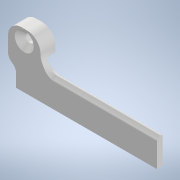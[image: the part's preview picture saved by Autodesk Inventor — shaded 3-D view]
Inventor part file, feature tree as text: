
AUTODESK INVENTOR PART (.ipt)
format: ipt  version: 2022 (Build 260153000, 153)  size: 229,888 bytes
history: native  units: mm
features: reference x7, other x6, fillet x5, extrude x3, sketch x3, chamfer x1, projected_geometry x1
ambient origin geometry x8: Origin, YZ Plane, XZ Plane, XY Plane, X Axis, Y Axis, Z Axis, Center Point
bodies: Body1 (feature_tree)
feature tree (26):
  other  "Твердое тело1"
  extrude  "Выдавливание1"  Depth=1.0mm
  extrude  "Выдавливание2"  Depth=1.0mm
  fillet  "Сопряжение1"  Radius=3.0mm
  chamfer  "Фаска1"  Distance=4.0mm
  extrude  "Выдавливание3"  Depth=12.0mm
  fillet  "Сопряжение2"  Radius=2.0mm
  fillet  "Сопряжение3"  Radius=1.0mm
  fillet  "Сопряжение4"  Radius=3.5mm
  fillet  "Сопряжение5"  Radius=5.0mm
  sketch  "Эскиз1"
  reference  "Ссылка1"
  reference  "Ссылка2"
  reference  "Ссылка3"
  reference  "Ссылка4"
  reference  "Ссылка5"
  sketch  "Эскиз2"
  projected_geometry  "Спроецированная петля1"
  reference  "Ссылка6"
  sketch  "Эскиз3"
  reference  "Ссылка7"
  other  "<userpath>\Documents\Git\MZCAT_2024\MZCAT_4.iam"
  other  "MZCAT_4.iam"
  other  "wifi module:1"
  other  "base:1"
  other  "CAT_protector:1"
